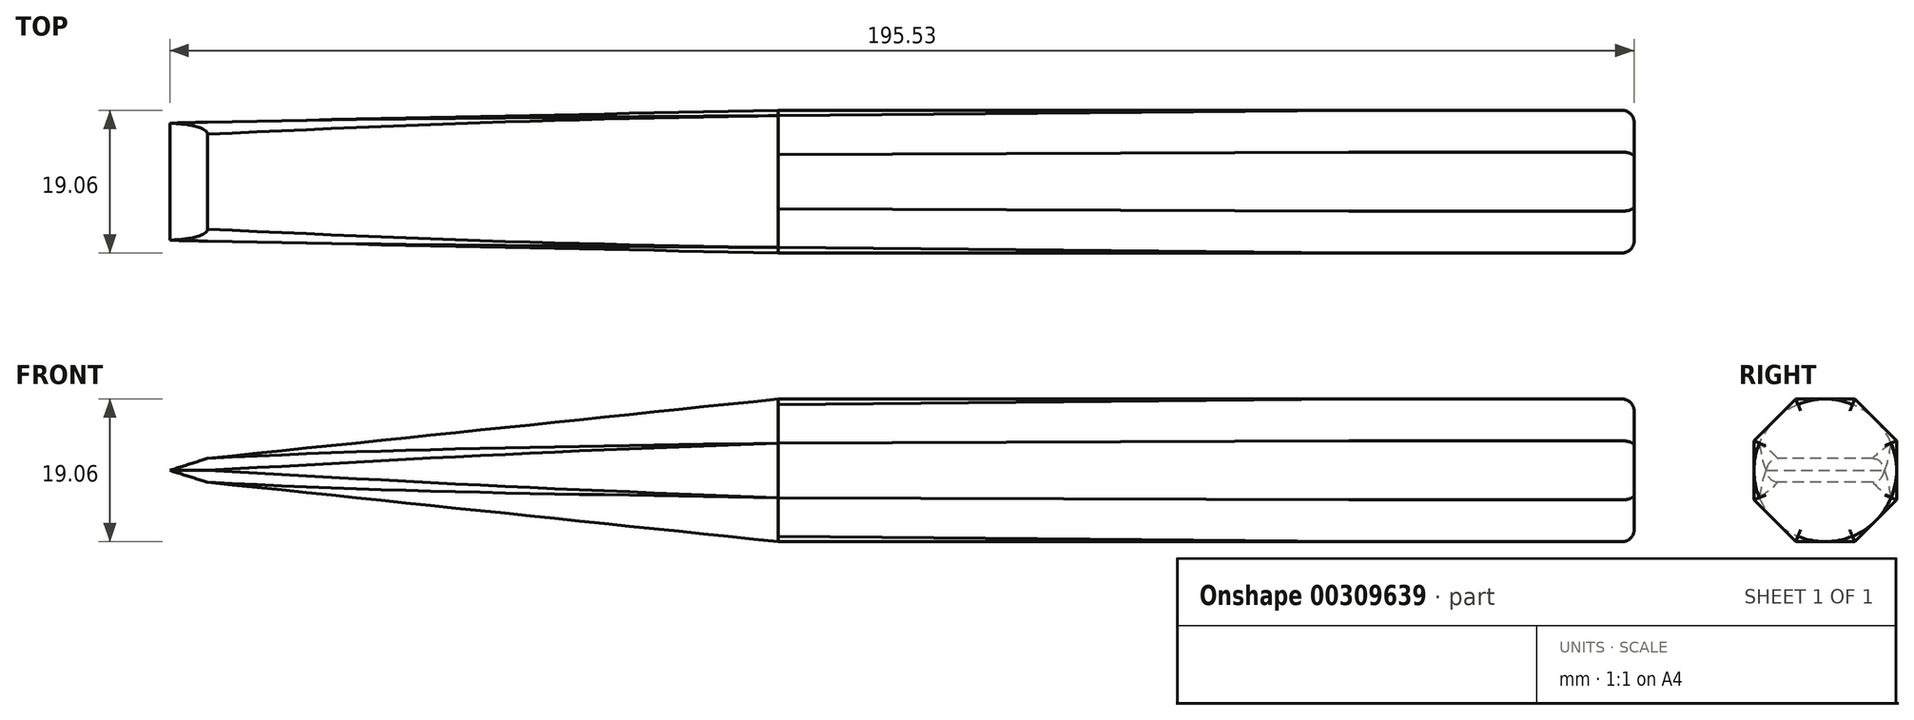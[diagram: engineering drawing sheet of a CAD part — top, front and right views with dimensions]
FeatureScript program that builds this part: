
annotation { "Feature Type Name" : "Feature", "Feature Type Description" : "" }
export const myFeature = defineFeature(function(context is Context, id is Id, definition is map)
    precondition{}
    {
        {
            var Q0;
            Q0=qCreatedBy(makeId("Right.planeOp"),FACE);
            var sketch = newSketch(context, id + "F0", { "sketchPlane" : qUnion([Q0])});
            skCircle(sketch, "E0.cCircle", {"center": v(0, 0) * mm, "radius": 9.53 * mm, "construction": true});
            skLineSegment(sketch, "E0.0", {"start": v(9.53, 3.95) * mm, "end": v(9.53, -3.95) * mm});
            skLineSegment(sketch, "E0.1", {"start": v(9.53, -3.95) * mm, "end": v(3.95, -9.53) * mm});
            skLineSegment(sketch, "E0.2", {"start": v(3.95, -9.53) * mm, "end": v(-3.95, -9.53) * mm});
            skLineSegment(sketch, "E0.3", {"start": v(-3.95, -9.53) * mm, "end": v(-9.53, -3.95) * mm});
            skLineSegment(sketch, "E0.4", {"start": v(-9.53, -3.95) * mm, "end": v(-9.53, 3.95) * mm});
            skLineSegment(sketch, "E0.5", {"start": v(-9.53, 3.95) * mm, "end": v(-3.95, 9.52) * mm});
            skLineSegment(sketch, "E0.6", {"start": v(-3.95, 9.52) * mm, "end": v(3.95, 9.53) * mm});
            skLineSegment(sketch, "E0.7", {"start": v(3.95, 9.53) * mm, "end": v(9.53, 3.95) * mm});
            skPoint(sketch, "E0.0.midPoint", {"position": v(9.53, 0) * mm});
            skSolve(sketch);
        }
        {
            var Q0;
            Q0=makeQuery(id+"F0.imprint","IMPRINT",FACE,{"disambiguationData":[TD([[makeQuery(id+"F0.imprint","IMPRINT",EDGE,{"derivedFrom":sQuery(id+"F0.wireOp",EDGE,"E0.0")}),-1.0]])]});
            extrude(context, id + "F1", {"entities" : qUnion([Q0]), "oppositeDirection" : true, "depth" : 38.1 * mm});
        }
        {
            var Q0;
            Q0=makeQuery(id+"F1.opExtrude","CAP_FACE",FACE,{"disambiguationData":[OSD([sQuery(id+"F0.wireOp",EDGE,"E0.0"),sQuery(id+"F0.wireOp",EDGE,"E0.1"),sQuery(id+"F0.wireOp",EDGE,"E0.2"),sQuery(id+"F0.wireOp",EDGE,"E0.3"),sQuery(id+"F0.wireOp",EDGE,"E0.4"),sQuery(id+"F0.wireOp",EDGE,"E0.5"),sQuery(id+"F0.wireOp",EDGE,"E0.6"),sQuery(id+"F0.wireOp",EDGE,"E0.7")])],"isStart":false});
            cPlane(context, id + "F2", {"entities" : qUnion([Q0]), "cplaneType" : CPlaneType.OFFSET, "offset" : 76.2 * mm, "width" : 152.4 * mm, "height" : 152.4 * mm});
        }
        {
            var Q0;
            Q0=qCreatedBy(id+"F2.planeOp",FACE);
            var sketch = newSketch(context, id + "F3", { "sketchPlane" : qUnion([Q0])});
            skCircle(sketch, "E1", {"center": v(0, 0) * mm, "radius": 9.53 * mm});
            skSolve(sketch);
        }
        {
            var Q1;
            Q1=makeQuery(id+"F1.opExtrude","CAP_FACE",FACE,{"disambiguationData":[OSD([sQuery(id+"F0.wireOp",EDGE,"E0.0"),sQuery(id+"F0.wireOp",EDGE,"E0.1"),sQuery(id+"F0.wireOp",EDGE,"E0.2"),sQuery(id+"F0.wireOp",EDGE,"E0.3"),sQuery(id+"F0.wireOp",EDGE,"E0.4"),sQuery(id+"F0.wireOp",EDGE,"E0.5"),sQuery(id+"F0.wireOp",EDGE,"E0.6"),sQuery(id+"F0.wireOp",EDGE,"E0.7")])],"isStart":false});
            var Q2;
            Q2=makeQuery(id+"F3.imprint","IMPRINT",FACE,{"disambiguationData":[TD([[makeQuery(id+"F3.imprint","IMPRINT",EDGE,{"derivedFrom":sQuery(id+"F3.wireOp",EDGE,"E1")}),1.0]])]});
            loft(context, id + "F4", {"operationType" : NewBodyOperationType.ADD, "sheetProfilesArray" : [{ "sheetProfileEntities" : qUnion([Q1]) }, { "sheetProfileEntities" : qUnion([Q2]) }]});
        }
        {
            var Q0;
            Q0=makeQuery(id+"F4.opLoft","CAP_FACE",FACE,{"disambiguationData":[OSD([makeQuery(id+"F3.imprint","IMPRINT",FACE,{"disambiguationData":[TD([[makeQuery(id+"F3.imprint","IMPRINT",EDGE,{"derivedFrom":sQuery(id+"F3.wireOp",EDGE,"E1")}),1.0]])]})])],"isStart":true});
            cPlane(context, id + "F5", {"entities" : qUnion([Q0]), "cplaneType" : CPlaneType.OFFSET, "offset" : 76.2 * mm, "width" : 152.4 * mm, "height" : 152.4 * mm});
        }
        {
            var Q0;
            Q0=qCreatedBy(id+"F5.planeOp",FACE);
            var sketch = newSketch(context, id + "F6", { "sketchPlane" : qUnion([Q0])});
            skLineSegment(sketch, "E2.bottom", {"start": v(-7.94, 1.59) * mm, "end": v(7.94, 1.59) * mm});
            skLineSegment(sketch, "E2.top", {"start": v(-7.94, -1.59) * mm, "end": v(7.94, -1.59) * mm});
            skLineSegment(sketch, "E2.left", {"start": v(-7.94, 1.59) * mm, "end": v(-7.94, -1.59) * mm});
            skLineSegment(sketch, "E2.right", {"start": v(7.94, 1.59) * mm, "end": v(7.94, -1.59) * mm});
            skSolve(sketch);
        }
        {
            var Q0;
            Q0=qCreatedBy(id+"F2.planeOp",FACE);
            var sketch = newSketch(context, id + "F7", { "sketchPlane" : qUnion([Q0])});
            skLineSegment(sketch, "E3", {"start": v(0, 0) * mm, "end": v(-8.8, 3.65) * mm, "construction": true});
            skLineSegment(sketch, "E4", {"start": v(0, 0) * mm, "end": v(8.8, -3.65) * mm, "construction": true});
            skLineSegment(sketch, "E5", {"start": v(0, 0) * mm, "end": v(8.8, 3.65) * mm, "construction": true});
            skLineSegment(sketch, "E6", {"start": v(0, 0) * mm, "end": v(-8.8, -3.65) * mm, "construction": true});
            skLineSegment(sketch, "E7", {"start": v(0, 0) * mm, "end": v(0, 9.53) * mm, "construction": true});
            skArc(sketch, "E8", {"start": v(-8.8, 3.65) * mm, "mid": v(-9.53, 0) * mm, "end": v(-8.8, -3.65) * mm});
            skLineSegment(sketch, "E9", {"start": v(-8.8, -3.65) * mm, "end": v(-8.8, -3.65) * mm});
            skArc(sketch, "E10", {"start": v(-8.8, -3.65) * mm, "mid": v(0, -9.53) * mm, "end": v(8.8, -3.65) * mm});
            skLineSegment(sketch, "E11", {"start": v(8.8, -3.65) * mm, "end": v(8.8, -3.65) * mm});
            skArc(sketch, "E12", {"start": v(8.8, -3.65) * mm, "mid": v(9.53, 0) * mm, "end": v(8.8, 3.65) * mm});
            skArc(sketch, "E13", {"start": v(8.8, 3.65) * mm, "mid": v(0, 9.53) * mm, "end": v(-8.8, 3.65) * mm});
            skSolve(sketch);
        }
        {
            var Q1;
            Q1=makeQuery(id+"F6.imprint","IMPRINT",FACE,{"disambiguationData":[TD([[makeQuery(id+"F6.imprint","IMPRINT",EDGE,{"derivedFrom":sQuery(id+"F6.wireOp",EDGE,"E2.bottom")}),-1.0]])]});
            var Q2;
            Q2 = qSketchRegion(id + "F7", true);
            loft(context, id + "F8", {"operationType" : NewBodyOperationType.ADD, "sheetProfilesArray" : [{ "sheetProfileEntities" : qUnion([Q1]) }, { "sheetProfileEntities" : qUnion([Q2]) }]});
        }
        {
            var Q0;
            Q0=qCreatedBy(makeId("Front.planeOp"),FACE);
            var sketch = newSketch(context, id + "F9", { "sketchPlane" : qUnion([Q0])});
            skLineSegment(sketch, "E14", {"start": v(-195.53, 0) * mm, "end": v(-190.5, 1.59) * mm});
            skLineSegment(sketch, "E15", {"start": v(-190.5, 1.59) * mm, "end": v(-190.5, -1.59) * mm});
            skLineSegment(sketch, "E16", {"start": v(-190.5, -1.59) * mm, "end": v(-195.53, 0) * mm});
            skSolve(sketch);
        }
        {
            var Q0;
            Q0=makeQuery(id+"F9.imprint","IMPRINT",FACE,{"disambiguationData":[TD([[makeQuery(id+"F9.imprint","IMPRINT",EDGE,{"derivedFrom":sQuery(id+"F9.wireOp",EDGE,"E14")}),-1.0]])]});
            extrude(context, id + "F10", {"entities" : qUnion([Q0]), "operationType" : NewBodyOperationType.ADD, "endBound" : BoundingType.SYMMETRIC, "depth" : 15.88 * mm});
        }
        {
            var Q0;
            Q0=makeQuery(id+"F10.opExtrude","CAP_EDGE",EDGE,{"disambiguationData":[OSD([sQuery(id+"F9.wireOp",EDGE,"E14")])],"isStart":true});
            var Q1;
            Q1=makeQuery(id+"F10.opExtrude","CAP_EDGE",EDGE,{"disambiguationData":[OSD([sQuery(id+"F9.wireOp",EDGE,"E16")])],"isStart":true});
            var Q2;
            Q2=makeQuery(id+"F8.opLoft","SWEPT_EDGE",EDGE,{"disambiguationData":[OSD([sQuery(id+"F6.wireOp",EDGE,"E2.bottom"),sQuery(id+"F6.wireOp",EDGE,"E2.left"),sQuery(id+"F7.wireOp",EDGE,"E8"),sQuery(id+"F7.wireOp",EDGE,"E13")])]});
            var Q3;
            Q3=makeQuery(id+"F8.opLoft","SWEPT_EDGE",EDGE,{"disambiguationData":[OSD([sQuery(id+"F6.wireOp",EDGE,"E2.top"),sQuery(id+"F6.wireOp",EDGE,"E2.left"),sQuery(id+"F7.wireOp",EDGE,"E8"),sQuery(id+"F7.wireOp",EDGE,"E10")])]});
            var Q4;
            Q4=makeQuery(id+"F8.opLoft","SWEPT_EDGE",EDGE,{"disambiguationData":[OSD([sQuery(id+"F6.wireOp",EDGE,"E2.bottom"),sQuery(id+"F6.wireOp",EDGE,"E2.right"),sQuery(id+"F7.wireOp",EDGE,"E12"),sQuery(id+"F7.wireOp",EDGE,"E13")])]});
            var Q5;
            Q5=makeQuery(id+"F10.opExtrude","CAP_EDGE",EDGE,{"disambiguationData":[OSD([sQuery(id+"F9.wireOp",EDGE,"E14")])],"isStart":false});
            var Q6;
            Q6=makeQuery(id+"F8.opLoft","SWEPT_EDGE",EDGE,{"disambiguationData":[OSD([sQuery(id+"F6.wireOp",EDGE,"E2.top"),sQuery(id+"F6.wireOp",EDGE,"E2.right"),sQuery(id+"F7.wireOp",EDGE,"E10"),sQuery(id+"F7.wireOp",EDGE,"E12")])]});
            var Q7;
            Q7=makeQuery(id+"F10.opExtrude","CAP_EDGE",EDGE,{"disambiguationData":[OSD([sQuery(id+"F9.wireOp",EDGE,"E16")])],"isStart":false});
            fillet(context, id + "F11", {"entities" : qUnion([Q0, Q1, Q2, Q3, Q4, Q5, Q6, Q7]), "radius" : 1.59 * mm, "tangentPropagation" : true, "allowEdgeOverflow" : false});
        }
        {
            var Q0;
            Q0=makeQuery(id+"F1.opExtrude","CAP_FACE",FACE,{"disambiguationData":[OSD([sQuery(id+"F0.wireOp",EDGE,"E0.0"),sQuery(id+"F0.wireOp",EDGE,"E0.1"),sQuery(id+"F0.wireOp",EDGE,"E0.2"),sQuery(id+"F0.wireOp",EDGE,"E0.3"),sQuery(id+"F0.wireOp",EDGE,"E0.4"),sQuery(id+"F0.wireOp",EDGE,"E0.5"),sQuery(id+"F0.wireOp",EDGE,"E0.6"),sQuery(id+"F0.wireOp",EDGE,"E0.7")])],"isStart":true});
            fillet(context, id + "F12", {"entities" : qUnion([Q0]), "radius" : 1.59 * mm, "tangentPropagation" : true, "allowEdgeOverflow" : false});
        }
    });
